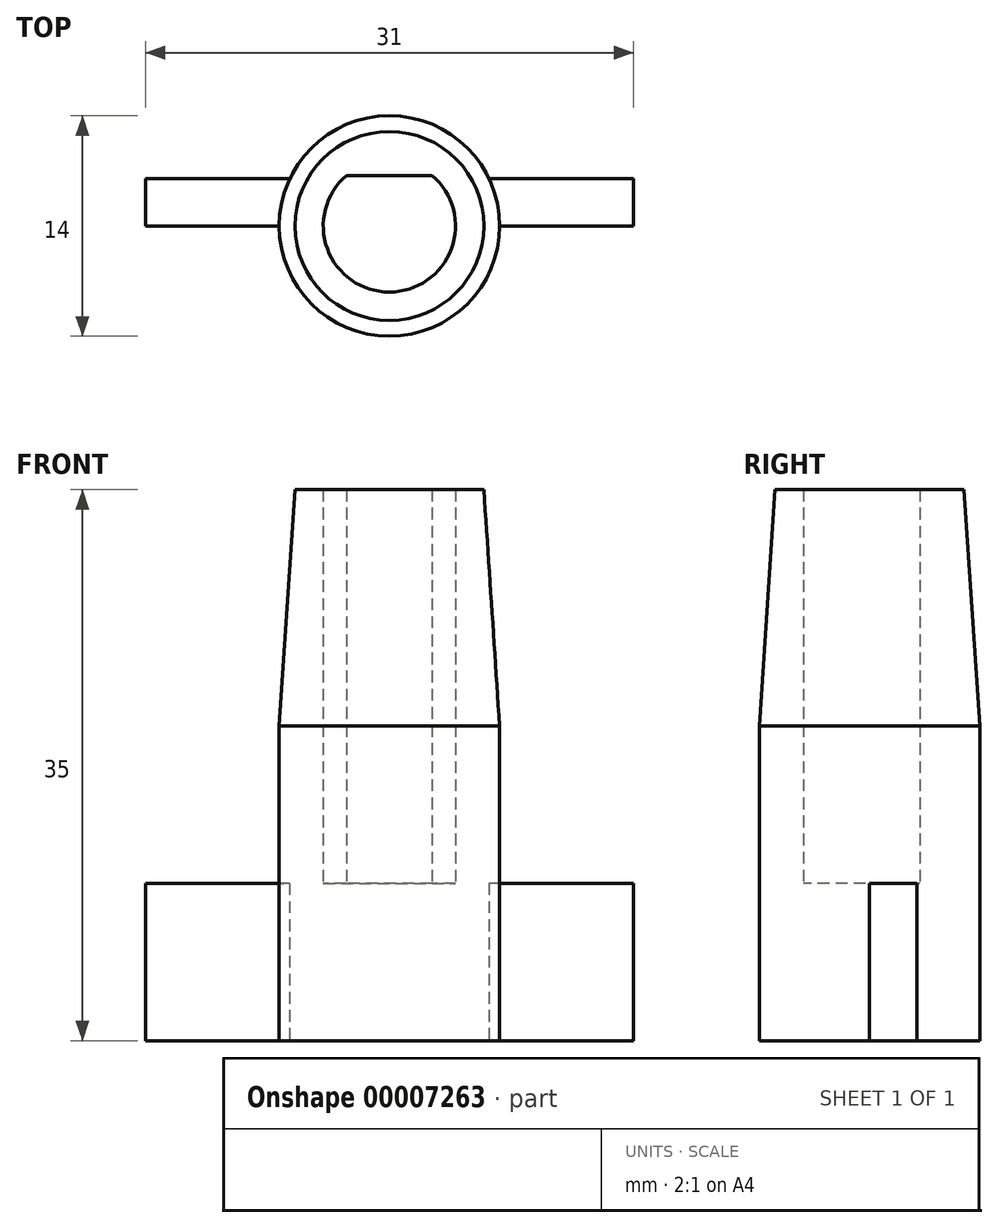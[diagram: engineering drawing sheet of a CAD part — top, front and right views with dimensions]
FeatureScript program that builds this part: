
annotation { "Feature Type Name" : "Feature", "Feature Type Description" : "" }
export const myFeature = defineFeature(function(context is Context, id is Id, definition is map)
    precondition{}
    {
        {
            var Q0;
            Q0=qCreatedBy(makeId("Top.planeOp"),FACE);
            var sketch = newSketch(context, id + "F0", { "sketchPlane" : qUnion([Q0])});
            skArc(sketch, "E0", {"start": v(-7, 0) * mm, "mid": v(0, -7) * mm, "end": v(7, 0) * mm});
            skLineSegment(sketch, "E1", {"start": v(-7, 0) * mm, "end": v(-15.5, 0) * mm});
            skLineSegment(sketch, "E2", {"start": v(-15.5, 0) * mm, "end": v(-15.5, 3) * mm});
            skLineSegment(sketch, "E3", {"start": v(-15.5, 3) * mm, "end": v(-6.32, 3) * mm});
            skLineSegment(sketch, "E4", {"start": v(7, 0) * mm, "end": v(15.5, 0) * mm});
            skLineSegment(sketch, "E5", {"start": v(15.5, 0) * mm, "end": v(15.5, 3) * mm});
            skLineSegment(sketch, "E6", {"start": v(15.5, 3) * mm, "end": v(6.32, 3) * mm});
            skArc(sketch, "E7.trimOffspring", {"start": v(6.32, 3) * mm, "mid": v(0, 7) * mm, "end": v(-6.32, 3) * mm});
            skSolve(sketch);
        }
        {
            var Q0;
            Q0 = qSketchRegion(id + "F0", true);
            extrude(context, id + "F1", {"entities" : qUnion([Q0]), "depth" : 10 * mm});
        }
        {
            var Q0;
            Q0=makeQuery(id+"F1.opExtrude","CAP_FACE",FACE,{"disambiguationData":[OSD([sQuery(id+"F0.wireOp",EDGE,"ed448936-c796-4095-90f0-5d46e5889457"),sQuery(id+"F0.wireOp",EDGE,"E0")])],"isStart":false});
            var sketch = newSketch(context, id + "F2", { "sketchPlane" : qUnion([Q0])});
            skArc(sketch, "E8", {"start": v(-2.72, 3.2) * mm, "mid": v(0, -4.2) * mm, "end": v(2.72, 3.2) * mm});
            skLineSegment(sketch, "E9", {"start": v(2.72, 3.2) * mm, "end": v(-2.72, 3.2) * mm});
            skCircle(sketch, "E10.0", {"center": v(0, 0) * mm, "radius": 7 * mm});
            skSolve(sketch);
        }
        {
            var Q0;
            Q0 = qSketchRegion(id + "F2", true);
            extrude(context, id + "F3", {"entities" : qUnion([Q0]), "operationType" : NewBodyOperationType.ADD, "depth" : 25 * mm});
        }
        {
            var Q0;
            Q0=makeQuery(id+"F3.opExtrude","CAP_EDGE",EDGE,{"disambiguationData":[OSD([sQuery(id+"F2.wireOp",EDGE,"E10.0")])],"isStart":false});
            chamfer(context, id + "F4", {"entities" : qUnion([Q0]), "chamferType" : ChamferType.TWO_OFFSETS, "width1" : 1 * mm, "oppositeDirection" : false, "width2" : 15 * mm, "tangentPropagation" : true});
        }
    });
